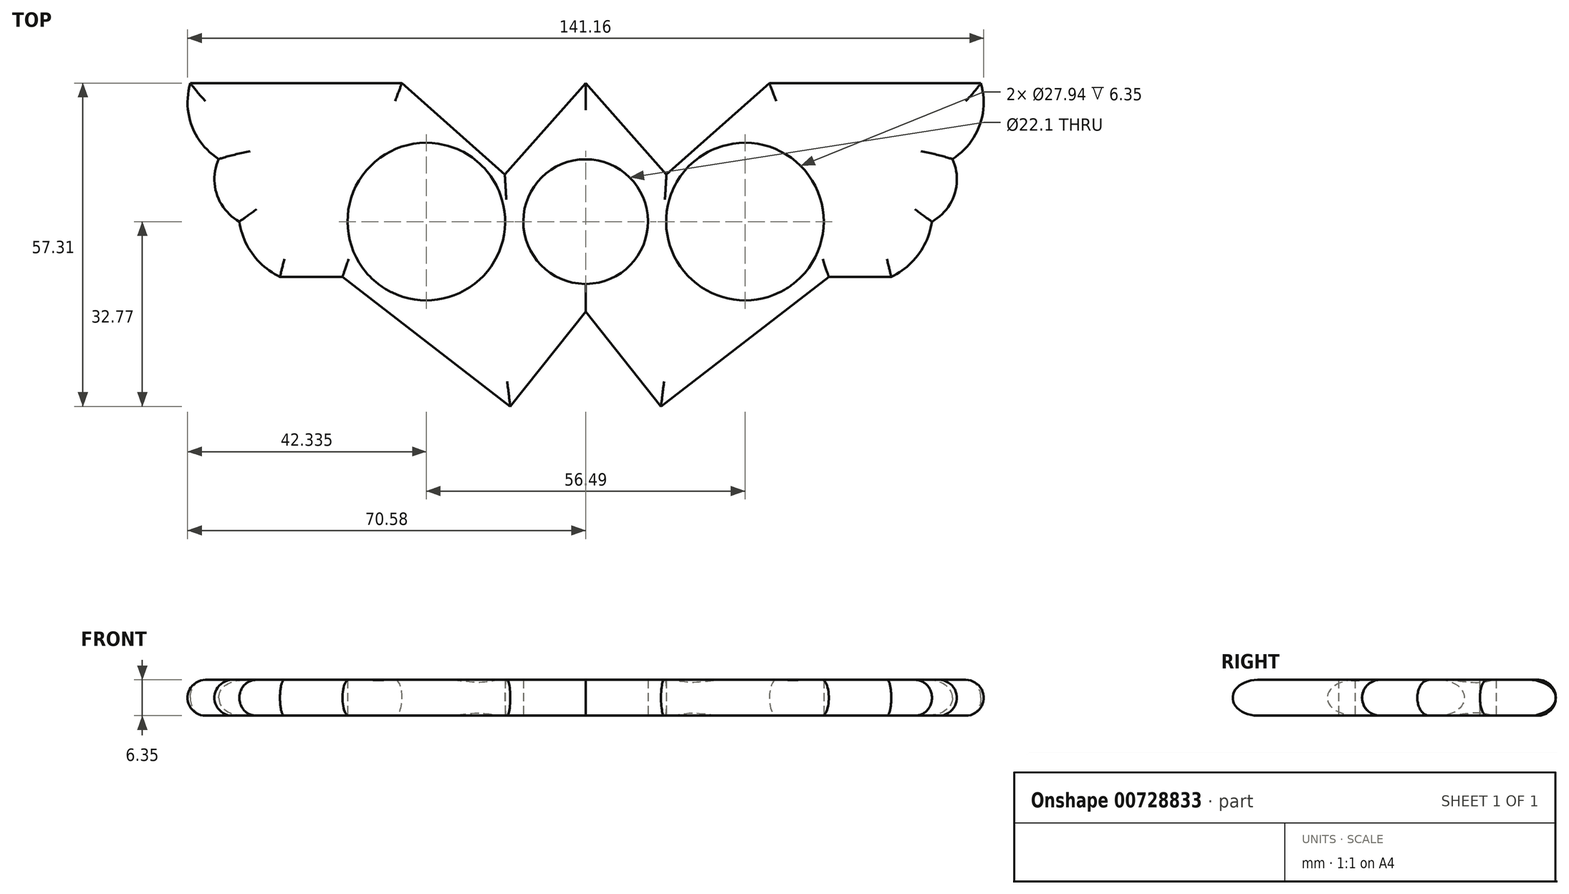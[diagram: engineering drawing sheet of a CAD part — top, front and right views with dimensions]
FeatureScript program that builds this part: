
annotation { "Feature Type Name" : "Feature", "Feature Type Description" : "" }
export const myFeature = defineFeature(function(context is Context, id is Id, definition is map)
    precondition{}
    {
        {
            var Q0;
            Q0=qCreatedBy(makeId("Top.planeOp"),FACE);
            var sketch = newSketch(context, id + "F0", { "sketchPlane" : qUnion([Q0])});
            skCircle(sketch, "E0", {"center": v(0, 0) * mm, "radius": 11.05 * mm});
            skCircle(sketch, "E1", {"center": v(-28.24, 0) * mm, "radius": 11.05 * mm});
            skLineSegment(sketch, "E2", {"start": v(0, 24.54) * mm, "end": v(-14.33, 8.37) * mm});
            skLineSegment(sketch, "E3", {"start": v(-14.33, 8.37) * mm, "end": v(-32.58, 24.54) * mm});
            skLineSegment(sketch, "E4", {"start": v(-32.58, 24.54) * mm, "end": v(-56.32, 24.54) * mm});
            skLineSegment(sketch, "E5.MirrorCS", {"start": v(0, 24.54) * mm, "end": v(14.33, 8.37) * mm});
            skLineSegment(sketch, "E6.MirrorCS", {"start": v(32.58, 24.54) * mm, "end": v(56.32, 24.54) * mm});
            skLineSegment(sketch, "E7.MirrorCS", {"start": v(14.33, 8.37) * mm, "end": v(32.58, 24.54) * mm});
            skCircle(sketch, "E8.MirrorC", {"center": v(28.24, 0) * mm, "radius": 11.05 * mm});
            skLineSegment(sketch, "E9.1.0.1", {"start": v(-14.14, -13.63) * mm, "end": v(-18.37, -9.88) * mm});
            skLineSegment(sketch, "E9.1.0.3", {"start": v(8.6, -6.95) * mm, "end": v(14.51, -13.63) * mm});
            skLineSegment(sketch, "E9.1.0.4", {"start": v(14.51, -13.63) * mm, "end": v(18.55, -10.06) * mm});
            skPoint(sketch, "E10.orphan", {"position": v(32.77, 2.54) * mm});
            skLineSegment(sketch, "E11", {"start": v(39.4, 8.41) * mm, "end": v(42.4, 11.07) * mm});
            skLineSegment(sketch, "E12", {"start": v(42.4, 11.07) * mm, "end": v(51.59, 11.08) * mm});
            skCircle(sketch, "E13", {"center": v(28.24, 0) * mm, "radius": 13.97 * mm});
            skCircle(sketch, "E14", {"center": v(-28.24, 0) * mm, "radius": 13.97 * mm});
            skLineSegment(sketch, "E15", {"start": v(42.21, 0) * mm, "end": v(51.59, 0) * mm});
            skLineSegment(sketch, "E16", {"start": v(51.59, 11.08) * mm, "end": v(51.59, 11.08) * mm});
            skLineSegment(sketch, "E17", {"start": v(56.32, 24.54) * mm, "end": v(70.09, 24.54) * mm});
            skLineSegment(sketch, "E18", {"start": v(51.59, 11.08) * mm, "end": v(65.04, 11.1) * mm});
            skArc(sketch, "E19", {"start": v(65.04, 11.1) * mm, "mid": v(69.82, 16.97) * mm, "end": v(70.09, 24.54) * mm});
            skArc(sketch, "E20", {"start": v(61.4, 0) * mm, "mid": v(65.39, 4.84) * mm, "end": v(65.04, 11.1) * mm});
            skLineSegment(sketch, "E21.MirrorCS", {"start": v(-39.4, 8.41) * mm, "end": v(-42.4, 11.07) * mm});
            skLineSegment(sketch, "E22.MirrorCS", {"start": v(-42.4, 11.07) * mm, "end": v(-51.59, 11.08) * mm});
            skLineSegment(sketch, "E23.MirrorCS", {"start": v(-51.59, 11.08) * mm, "end": v(-51.59, 11.08) * mm});
            skLineSegment(sketch, "E24.MirrorCS", {"start": v(-51.59, 11.08) * mm, "end": v(-65.04, 11.1) * mm});
            skLineSegment(sketch, "E25.MirrorCS", {"start": v(-56.32, 24.54) * mm, "end": v(-70.09, 24.54) * mm});
            skArc(sketch, "E26.MirrorCS", {"start": v(-65.04, 11.1) * mm, "mid": v(-69.82, 16.97) * mm, "end": v(-70.09, 24.54) * mm});
            skArc(sketch, "E27.MirrorCS", {"start": v(-61.4, 0) * mm, "mid": v(-65.39, 4.84) * mm, "end": v(-65.04, 11.1) * mm});
            skLineSegment(sketch, "E28.1.0.0", {"start": v(0, -15.96) * mm, "end": v(-13.37, -32.77) * mm});
            skLineSegment(sketch, "E28.1.0.3", {"start": v(-43.11, -9.81) * mm, "end": v(-54.19, -9.81) * mm});
            skLineSegment(sketch, "E28.1.0.4", {"start": v(-52.8, -9.4) * mm, "end": v(-54.19, -9.81) * mm});
            skLineSegment(sketch, "E29", {"start": v(51.59, 0) * mm, "end": v(61.4, 0) * mm});
            skLineSegment(sketch, "E30.MirrorCS", {"start": v(-51.59, 0) * mm, "end": v(-61.4, 0) * mm});
            skLineSegment(sketch, "E31.MirrorCS", {"start": v(-42.21, 0) * mm, "end": v(-51.59, 0) * mm});
            skArc(sketch, "E32.MirrorCS", {"start": v(-54.19, -9.81) * mm, "mid": v(-59.02, -5.8) * mm, "end": v(-61.4, 0) * mm});
            skPoint(sketch, "E33.orphan", {"position": v(58.34, -6.26) * mm});
            skPoint(sketch, "E34.orphan", {"position": v(-65.12, -13.12) * mm});
            skLineSegment(sketch, "E35.trimOffspring", {"start": v(-8.41, -7.16) * mm, "end": v(-14.14, -13.63) * mm});
            skPoint(sketch, "E36.orphan", {"position": v(0.19, 2.54) * mm});
            skPoint(sketch, "E37.orphan", {"position": v(-32.77, 2.54) * mm});
            skPoint(sketch, "E38.orphan", {"position": v(-32.4, 2.54) * mm});
            skLineSegment(sketch, "E39.trimOffspring", {"start": v(-56.16, 0) * mm, "end": v(-56.13, 2.54) * mm, "construction": true});
            skLineSegment(sketch, "E40", {"start": v(-61.4, 0) * mm, "end": v(-42.21, 0) * mm});
            skLineSegment(sketch, "E41", {"start": v(42.21, 0) * mm, "end": v(61.4, 0) * mm});
            skPoint(sketch, "E28.1.0.7.end.orphan", {"position": v(59.36, -13.37) * mm});
            skPoint(sketch, "E28.1.0.8.start.orphan", {"position": v(50.04, -13.37) * mm});
            skPoint(sketch, "E42.start.orphan", {"position": v(54.19, -9.81) * mm});
            skLineSegment(sketch, "E43.MirrorCS", {"start": v(0, -15.96) * mm, "end": v(13.37, -32.77) * mm});
            skLineSegment(sketch, "E44.MirrorCS", {"start": v(43.11, -9.81) * mm, "end": v(54.19, -9.81) * mm});
            skArc(sketch, "E45.MirrorCS", {"start": v(54.19, -9.81) * mm, "mid": v(59.02, -5.8) * mm, "end": v(61.4, 0) * mm});
            skPoint(sketch, "E28.1.0.2.start.orphan", {"position": v(-27.1, -21.7) * mm});
            skPoint(sketch, "E28.1.0.1.end.orphan", {"position": v(-27.42, -21.7) * mm});
            skPoint(sketch, "E46.MirrorCS.end.orphan", {"position": v(27.42, -21.7) * mm});
            skPoint(sketch, "E46.MirrorCS.start.orphan", {"position": v(13.37, -32.77) * mm});
            skPoint(sketch, "E47.MirrorCS.end.orphan", {"position": v(43.11, -9.81) * mm});
            skPoint(sketch, "E47.MirrorCS.start.orphan", {"position": v(27.1, -21.7) * mm});
            skLineSegment(sketch, "E48", {"start": v(-43.11, -9.81) * mm, "end": v(-13.37, -32.77) * mm});
            skLineSegment(sketch, "E49.MirrorCS", {"start": v(43.11, -9.81) * mm, "end": v(13.37, -32.77) * mm});
            skSolve(sketch);
        }
        {
            var Q0;
            Q0 = qSketchRegion(id + "F0", true);
            extrude(context, id + "F1", {"entities" : qUnion([Q0]), "depth" : 6.35 * mm, "offsetDistance" : 25.4 * mm});
        }
        {
            var Q0;
            Q0=makeQuery(id+"F1.opExtrude","CAP_EDGE",EDGE,{"disambiguationData":[OSD([sQuery(id+"F0.wireOp",EDGE,"E4"),sQuery(id+"F0.wireOp",EDGE,"E25.MirrorCS")])],"isStart":false});
            var Q1;
            Q1=makeQuery(id+"F1.opExtrude","CAP_EDGE",EDGE,{"disambiguationData":[OSD([sQuery(id+"F0.wireOp",EDGE,"E27.MirrorCS")])],"isStart":false});
            var Q2;
            Q2=makeQuery(id+"F1.opExtrude","CAP_EDGE",EDGE,{"disambiguationData":[OSD([sQuery(id+"F0.wireOp",EDGE,"E32.MirrorCS")])],"isStart":false});
            var Q3;
            Q3=makeQuery(id+"F1.opExtrude","CAP_EDGE",EDGE,{"disambiguationData":[OSD([sQuery(id+"F0.wireOp",EDGE,"E28.1.0.3")])],"isStart":false});
            var Q4;
            Q4=makeQuery(id+"F1.opExtrude","CAP_EDGE",EDGE,{"disambiguationData":[OSD([sQuery(id+"F0.wireOp",EDGE,"E48")])],"isStart":false});
            var Q5;
            Q5=makeQuery(id+"F1.opExtrude","CAP_EDGE",EDGE,{"disambiguationData":[OSD([sQuery(id+"F0.wireOp",EDGE,"E28.1.0.0")])],"isStart":false});
            var Q6;
            Q6=makeQuery(id+"F1.opExtrude","CAP_EDGE",EDGE,{"disambiguationData":[OSD([sQuery(id+"F0.wireOp",EDGE,"E43.MirrorCS")])],"isStart":false});
            var Q7;
            Q7=makeQuery(id+"F1.opExtrude","CAP_EDGE",EDGE,{"disambiguationData":[OSD([sQuery(id+"F0.wireOp",EDGE,"E49.MirrorCS")])],"isStart":false});
            var Q8;
            Q8=makeQuery(id+"F1.opExtrude","CAP_EDGE",EDGE,{"disambiguationData":[OSD([sQuery(id+"F0.wireOp",EDGE,"E44.MirrorCS")])],"isStart":false});
            var Q9;
            Q9=makeQuery(id+"F1.opExtrude","CAP_EDGE",EDGE,{"disambiguationData":[OSD([sQuery(id+"F0.wireOp",EDGE,"E45.MirrorCS")])],"isStart":false});
            var Q10;
            Q10=makeQuery(id+"F1.opExtrude","CAP_EDGE",EDGE,{"disambiguationData":[OSD([sQuery(id+"F0.wireOp",EDGE,"E3")])],"isStart":false});
            var Q11;
            Q11=makeQuery(id+"F1.opExtrude","CAP_EDGE",EDGE,{"disambiguationData":[OSD([sQuery(id+"F0.wireOp",EDGE,"E2")])],"isStart":false});
            var Q12;
            Q12=makeQuery(id+"F1.opExtrude","CAP_EDGE",EDGE,{"disambiguationData":[OSD([sQuery(id+"F0.wireOp",EDGE,"E5.MirrorCS")])],"isStart":false});
            var Q13;
            Q13=makeQuery(id+"F1.opExtrude","CAP_EDGE",EDGE,{"disambiguationData":[OSD([sQuery(id+"F0.wireOp",EDGE,"E7.MirrorCS")])],"isStart":false});
            var Q14;
            Q14=makeQuery(id+"F1.opExtrude","CAP_EDGE",EDGE,{"disambiguationData":[OSD([sQuery(id+"F0.wireOp",EDGE,"E6.MirrorCS"),sQuery(id+"F0.wireOp",EDGE,"E17")])],"isStart":false});
            var Q15;
            Q15=makeQuery(id+"F1.opExtrude","CAP_EDGE",EDGE,{"disambiguationData":[OSD([sQuery(id+"F0.wireOp",EDGE,"E19")])],"isStart":false});
            var Q16;
            Q16=makeQuery(id+"F1.opExtrude","CAP_EDGE",EDGE,{"disambiguationData":[OSD([sQuery(id+"F0.wireOp",EDGE,"E6.MirrorCS"),sQuery(id+"F0.wireOp",EDGE,"E17")])],"isStart":true});
            var Q17;
            Q17=makeQuery(id+"F1.opExtrude","CAP_EDGE",EDGE,{"disambiguationData":[OSD([sQuery(id+"F0.wireOp",EDGE,"E7.MirrorCS")])],"isStart":true});
            var Q18;
            Q18=makeQuery(id+"F1.opExtrude","CAP_EDGE",EDGE,{"disambiguationData":[OSD([sQuery(id+"F0.wireOp",EDGE,"E26.MirrorCS")])],"isStart":true});
            var Q19;
            Q19=makeQuery(id+"F1.opExtrude","CAP_EDGE",EDGE,{"disambiguationData":[OSD([sQuery(id+"F0.wireOp",EDGE,"E32.MirrorCS")])],"isStart":true});
            var Q20;
            Q20=makeQuery(id+"F1.opExtrude","CAP_EDGE",EDGE,{"disambiguationData":[OSD([sQuery(id+"F0.wireOp",EDGE,"E28.1.0.3")])],"isStart":true});
            var Q21;
            Q21=makeQuery(id+"F1.opExtrude","CAP_EDGE",EDGE,{"disambiguationData":[OSD([sQuery(id+"F0.wireOp",EDGE,"E48")])],"isStart":true});
            var Q22;
            Q22=makeQuery(id+"F1.opExtrude","CAP_EDGE",EDGE,{"disambiguationData":[OSD([sQuery(id+"F0.wireOp",EDGE,"E28.1.0.0")])],"isStart":true});
            var Q23;
            Q23=makeQuery(id+"F1.opExtrude","CAP_EDGE",EDGE,{"disambiguationData":[OSD([sQuery(id+"F0.wireOp",EDGE,"E43.MirrorCS")])],"isStart":true});
            var Q24;
            Q24=makeQuery(id+"F1.opExtrude","CAP_EDGE",EDGE,{"disambiguationData":[OSD([sQuery(id+"F0.wireOp",EDGE,"E19")])],"isStart":true});
            var Q25;
            Q25=makeQuery(id+"F1.opExtrude","CAP_EDGE",EDGE,{"disambiguationData":[OSD([sQuery(id+"F0.wireOp",EDGE,"E49.MirrorCS")])],"isStart":true});
            var Q26;
            Q26=makeQuery(id+"F1.opExtrude","CAP_EDGE",EDGE,{"disambiguationData":[OSD([sQuery(id+"F0.wireOp",EDGE,"E44.MirrorCS")])],"isStart":true});
            var Q27;
            Q27=makeQuery(id+"F1.opExtrude","CAP_EDGE",EDGE,{"disambiguationData":[OSD([sQuery(id+"F0.wireOp",EDGE,"E45.MirrorCS")])],"isStart":true});
            var Q28;
            Q28=makeQuery(id+"F1.opExtrude","CAP_EDGE",EDGE,{"disambiguationData":[OSD([sQuery(id+"F0.wireOp",EDGE,"E20")])],"isStart":false});
            var Q29;
            Q29=makeQuery(id+"F1.opExtrude","CAP_EDGE",EDGE,{"disambiguationData":[OSD([sQuery(id+"F0.wireOp",EDGE,"E20")])],"isStart":true});
            var Q30;
            Q30=makeQuery(id+"F1.opExtrude","CAP_EDGE",EDGE,{"disambiguationData":[OSD([sQuery(id+"F0.wireOp",EDGE,"E2")])],"isStart":true});
            var Q31;
            Q31=makeQuery(id+"F1.opExtrude","CAP_EDGE",EDGE,{"disambiguationData":[OSD([sQuery(id+"F0.wireOp",EDGE,"E5.MirrorCS")])],"isStart":true});
            var Q32;
            Q32=makeQuery(id+"F1.opExtrude","CAP_EDGE",EDGE,{"disambiguationData":[OSD([sQuery(id+"F0.wireOp",EDGE,"E3")])],"isStart":true});
            var Q33;
            Q33=makeQuery(id+"F1.opExtrude","CAP_EDGE",EDGE,{"disambiguationData":[OSD([sQuery(id+"F0.wireOp",EDGE,"E4"),sQuery(id+"F0.wireOp",EDGE,"E25.MirrorCS")])],"isStart":true});
            var Q34;
            Q34=makeQuery(id+"F1.opExtrude","CAP_EDGE",EDGE,{"disambiguationData":[OSD([sQuery(id+"F0.wireOp",EDGE,"E27.MirrorCS")])],"isStart":true});
            var Q35;
            Q35=makeQuery(id+"F1.opExtrude","CAP_EDGE",EDGE,{"disambiguationData":[OSD([sQuery(id+"F0.wireOp",EDGE,"E26.MirrorCS")])],"isStart":false});
            fillet(context, id + "F2", {"entities" : qUnion([Q0, Q1, Q2, Q3, Q4, Q5, Q6, Q7, Q8, Q9, Q10, Q11, Q12, Q13, Q14, Q15, Q16, Q17, Q18, Q19, Q20, Q21, Q22, Q23, Q24, Q25, Q26, Q27, Q28, Q29, Q30, Q31, Q32, Q33, Q34, Q35]), "radius" : 3.17 * mm, "tangentPropagation" : true, "allowEdgeOverflow" : false});
        }
    });
